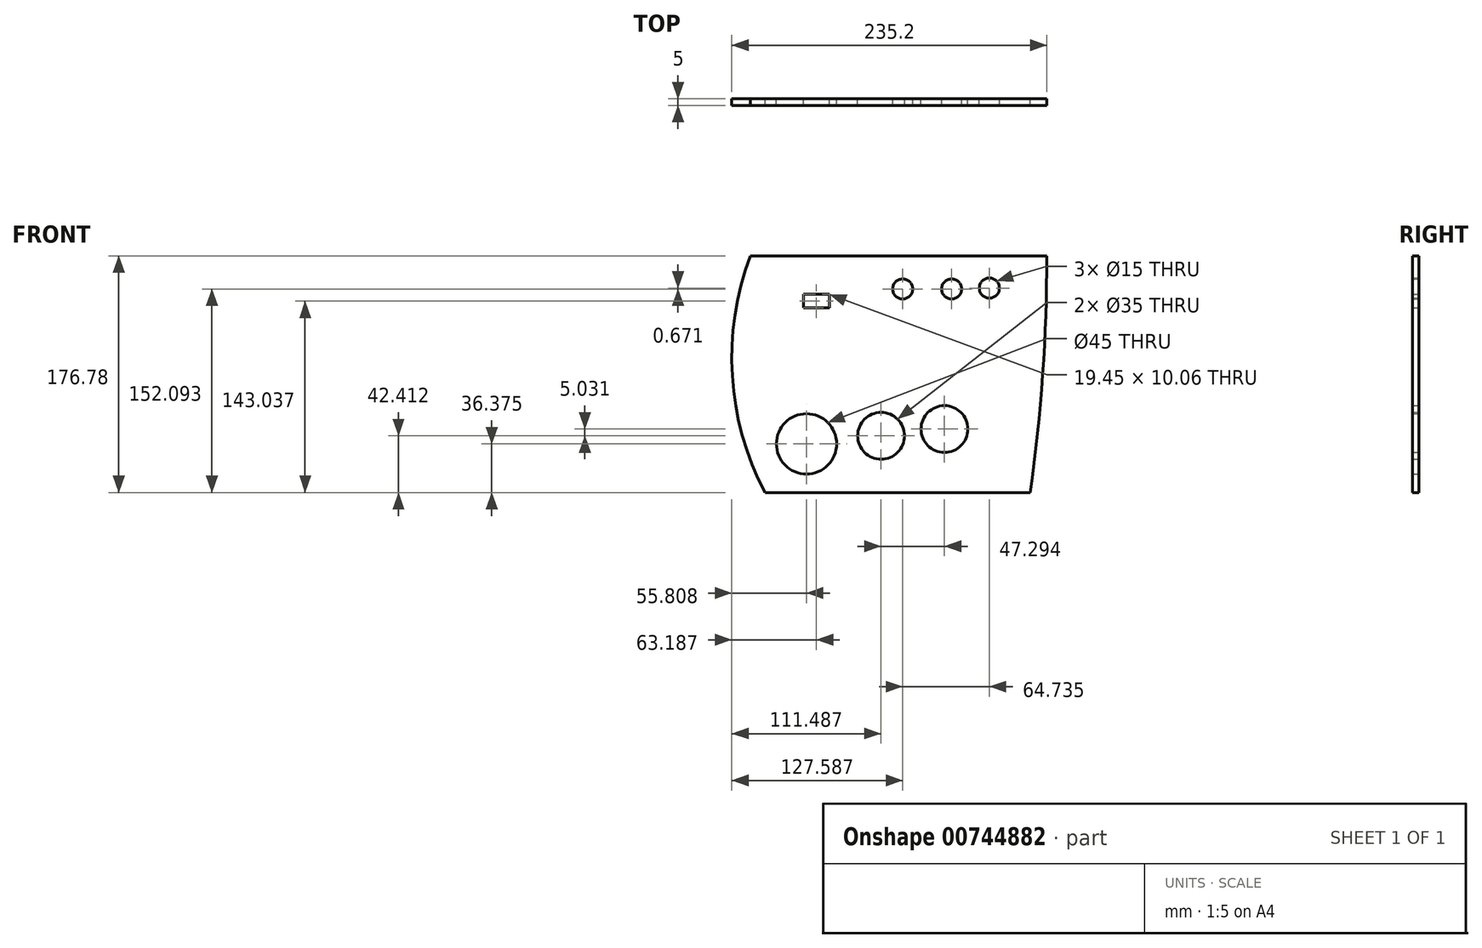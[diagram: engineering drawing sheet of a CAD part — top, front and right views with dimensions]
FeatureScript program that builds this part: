
annotation { "Feature Type Name" : "Feature", "Feature Type Description" : "" }
export const myFeature = defineFeature(function(context is Context, id is Id, definition is map)
    precondition{}
    {
        {
            var Q0;
            Q0=qCreatedBy(makeId("Front.planeOp"),FACE);
            var sketch = newSketch(context, id + "F0", { "sketchPlane" : qUnion([Q0])});
            skLineSegment(sketch, "E0.bottom", {"start": v(105.41, -88.4) * mm, "end": v(-92.5, -88.4) * mm});
            skLineSegment(sketch, "E0.top", {"start": v(117.86, 88.4) * mm, "end": v(-103.31, 88.4) * mm});
            skPoint(sketch, "E0.middle", {"position": v(0, 0) * mm});
            skArc(sketch, "E1", {"start": v(-103.31, 88.4) * mm, "mid": v(-116.94, -1.16) * mm, "end": v(-92.5, -88.4) * mm});
            skPoint(sketch, "E2.orphan", {"position": v(-117.86, 88.4) * mm});
            skPoint(sketch, "E3.orphan", {"position": v(-117.86, -88.4) * mm});
            skArc(sketch, "E4", {"start": v(105.41, -88.4) * mm, "mid": v(114.74, -0.22) * mm, "end": v(117.86, 88.4) * mm});
            skPoint(sketch, "E5.orphan", {"position": v(117.86, -88.4) * mm});
            skCircle(sketch, "E6", {"center": v(-61.53, -52.02) * mm, "radius": 22.5 * mm});
            skCircle(sketch, "E7", {"center": v(-5.85, -45.98) * mm, "radius": 17.5 * mm});
            skCircle(sketch, "E8", {"center": v(41.44, -40.95) * mm, "radius": 17.5 * mm});
            skCircle(sketch, "E9", {"center": v(10.25, 63.7) * mm, "radius": 7.5 * mm});
            skCircle(sketch, "E10", {"center": v(46.8, 63.7) * mm, "radius": 7.5 * mm});
            skCircle(sketch, "E11", {"center": v(74.98, 64.37) * mm, "radius": 7.5 * mm});
            skArc(sketch, "E12", {"start": v(65.93, 33.85) * mm, "mid": v(-8.77, 28.65) * mm, "end": v(-75.62, -5.06) * mm});
            skLineSegment(sketch, "E13.bottom", {"start": v(-44.43, 49.62) * mm, "end": v(-63.88, 49.62) * mm});
            skLineSegment(sketch, "E13.top", {"start": v(-44.43, 59.68) * mm, "end": v(-63.88, 59.68) * mm});
            skLineSegment(sketch, "E13.left", {"start": v(-44.43, 49.62) * mm, "end": v(-44.43, 59.68) * mm});
            skLineSegment(sketch, "E13.right", {"start": v(-63.88, 49.62) * mm, "end": v(-63.88, 59.68) * mm});
            skPoint(sketch, "E13.middle", {"position": v(-54.15, 54.65) * mm});
            skSolve(sketch);
        }
        {
            var Q0;
            Q0 = qSketchRegion(id + "F0", true);
            extrude(context, id + "F1", {"entities" : qUnion([Q0]), "depth" : 5 * mm, "offsetDistance" : 25 * mm});
        }
    });
